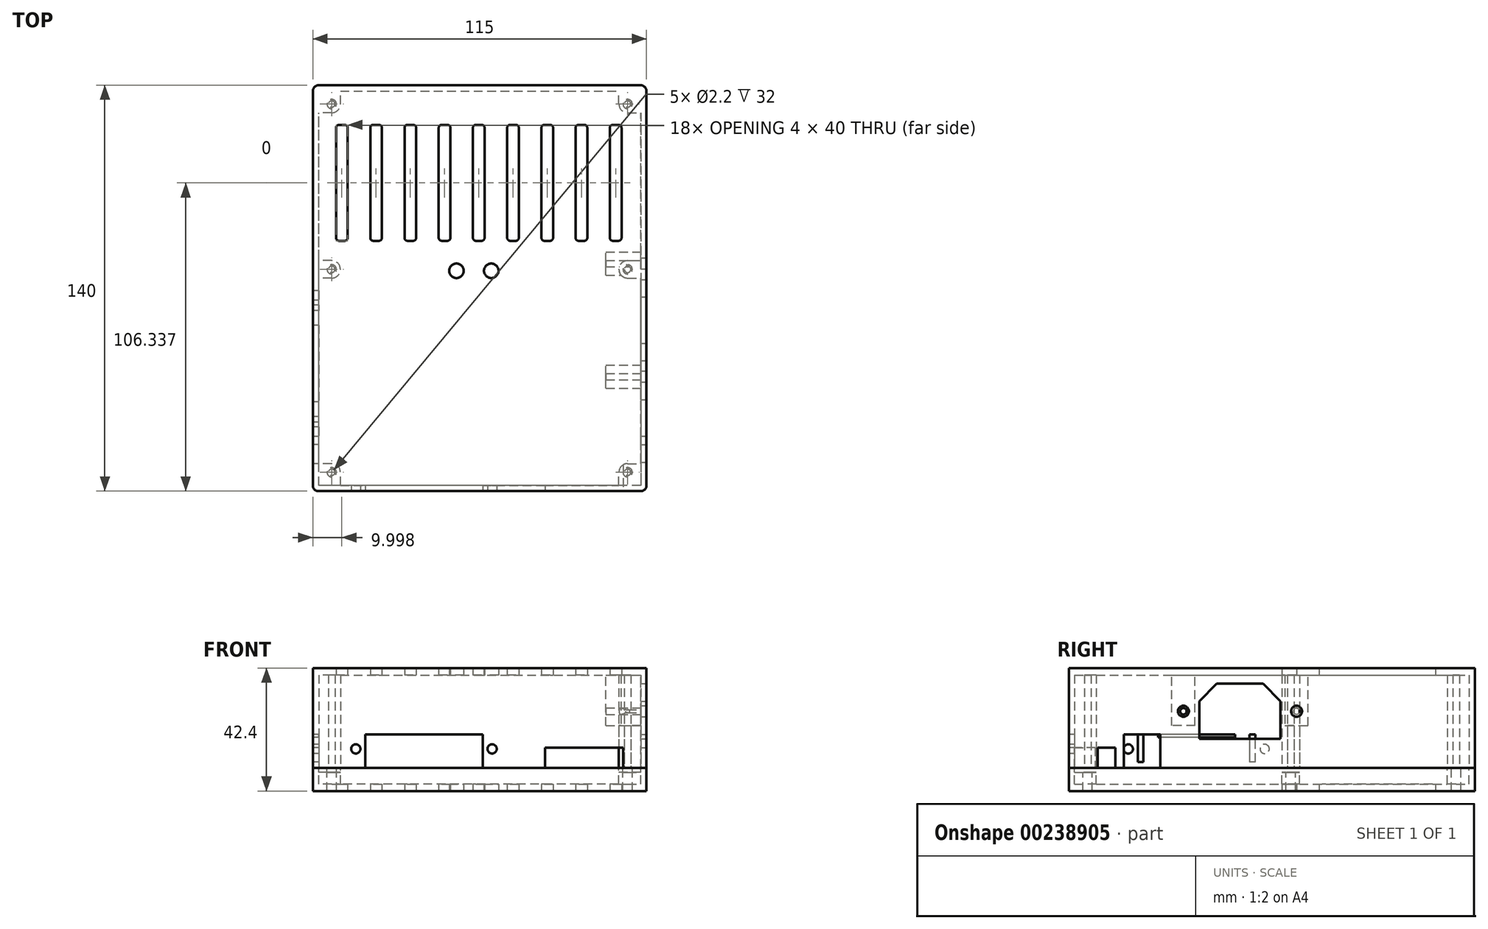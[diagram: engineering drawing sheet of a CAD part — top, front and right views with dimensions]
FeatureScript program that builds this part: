
annotation { "Feature Type Name" : "Feature", "Feature Type Description" : "" }
export const myFeature = defineFeature(function(context is Context, id is Id, definition is map)
    precondition{}
    {
        {
            var Q0;
            Q0=qCreatedBy(makeId("Top.planeOp"),FACE);
            var sketch = newSketch(context, id + "F0", { "sketchPlane" : qUnion([Q0])});
            skLineSegment(sketch, "E0.bottom", {"start": v(7.5, 0) * mm, "end": v(103.5, 0) * mm});
            skLineSegment(sketch, "E0.top", {"start": v(7.5, 136) * mm, "end": v(103.5, 136) * mm});
            skLineSegment(sketch, "E0.left", {"start": v(0, 7.5) * mm, "end": v(0, 71.5) * mm});
            skLineSegment(sketch, "E0.right", {"start": v(111, 7.5) * mm, "end": v(111, 71.5) * mm});
            skCircle(sketch, "E1", {"center": v(4.5, 4.5) * mm, "radius": 1.6 * mm, "construction": true});
            skLineSegment(sketch, "E2", {"start": v(55.5, 0) * mm, "end": v(55.5, 136) * mm, "construction": true});
            skCircle(sketch, "E3", {"center": v(4.5, 74.5) * mm, "radius": 1.6 * mm, "construction": true});
            skCircle(sketch, "E4", {"center": v(4.5, 131.5) * mm, "radius": 1.6 * mm, "construction": true});
            skCircle(sketch, "E5.MirrorC", {"center": v(106.5, 4.5) * mm, "radius": 1.6 * mm, "construction": true});
            skCircle(sketch, "E6.MirrorC", {"center": v(106.5, 74.5) * mm, "radius": 1.6 * mm, "construction": true});
            skCircle(sketch, "E7.MirrorC", {"center": v(106.5, 131.5) * mm, "radius": 1.6 * mm, "construction": true});
            skArc(sketch, "E8", {"start": v(7.5, 4.5) * mm, "mid": v(6.62, 6.62) * mm, "end": v(4.5, 7.5) * mm});
            skArc(sketch, "E9", {"start": v(4.5, 71.5) * mm, "mid": v(7.5, 74.5) * mm, "end": v(4.5, 77.5) * mm});
            skArc(sketch, "E10", {"start": v(4.5, 128.5) * mm, "mid": v(6.62, 129.38) * mm, "end": v(7.5, 131.5) * mm});
            skLineSegment(sketch, "E11", {"start": v(4.5, 7.5) * mm, "end": v(0, 7.5) * mm});
            skLineSegment(sketch, "E12", {"start": v(7.5, 0) * mm, "end": v(7.5, 4.5) * mm});
            skLineSegment(sketch, "E13.0", {"start": v(-2, 0) * mm, "end": v(-2, 136) * mm});
            skLineSegment(sketch, "E13.1", {"start": v(0, -2) * mm, "end": v(111, -2) * mm});
            skLineSegment(sketch, "E13.2", {"start": v(113, 0) * mm, "end": v(113, 136) * mm});
            skLineSegment(sketch, "E13.3", {"start": v(0, 138) * mm, "end": v(111, 138) * mm});
            skLineSegment(sketch, "E14", {"start": v(4.5, 77.5) * mm, "end": v(0, 77.5) * mm});
            skLineSegment(sketch, "E15", {"start": v(4.5, 71.5) * mm, "end": v(0, 71.5) * mm});
            skLineSegment(sketch, "E16", {"start": v(7.5, 131.5) * mm, "end": v(7.5, 136) * mm});
            skLineSegment(sketch, "E17", {"start": v(4.5, 128.5) * mm, "end": v(0, 128.5) * mm});
            skCircle(sketch, "E18", {"center": v(4.5, 4.5) * mm, "radius": 1.1 * mm});
            skCircle(sketch, "E19", {"center": v(4.5, 74.5) * mm, "radius": 1.1 * mm});
            skCircle(sketch, "E20", {"center": v(4.5, 131.5) * mm, "radius": 1.1 * mm});
            skLineSegment(sketch, "E21.MirrorCS", {"start": v(103.5, 0) * mm, "end": v(103.5, 4.5) * mm});
            skCircle(sketch, "E22.MirrorC", {"center": v(106.5, 4.5) * mm, "radius": 1.1 * mm});
            skArc(sketch, "E23.MirrorCS", {"start": v(103.5, 4.5) * mm, "mid": v(104.38, 6.62) * mm, "end": v(106.5, 7.5) * mm});
            skLineSegment(sketch, "E24.MirrorCS", {"start": v(106.5, 7.5) * mm, "end": v(111, 7.5) * mm});
            skLineSegment(sketch, "E25.MirrorCS", {"start": v(106.5, 71.5) * mm, "end": v(111, 71.5) * mm});
            skArc(sketch, "E26.MirrorCS", {"start": v(106.5, 71.5) * mm, "mid": v(103.5, 74.5) * mm, "end": v(106.5, 77.5) * mm});
            skCircle(sketch, "E27.MirrorC", {"center": v(106.5, 74.5) * mm, "radius": 1.1 * mm});
            skLineSegment(sketch, "E28.MirrorCS", {"start": v(106.5, 77.5) * mm, "end": v(111, 77.5) * mm});
            skLineSegment(sketch, "E29.MirrorCS", {"start": v(106.5, 128.5) * mm, "end": v(111, 128.5) * mm});
            skArc(sketch, "E30.MirrorCS", {"start": v(106.5, 128.5) * mm, "mid": v(104.38, 129.38) * mm, "end": v(103.5, 131.5) * mm});
            skLineSegment(sketch, "E31.MirrorCS", {"start": v(103.5, 131.5) * mm, "end": v(103.5, 136) * mm});
            skCircle(sketch, "E32.MirrorC", {"center": v(106.5, 131.5) * mm, "radius": 1.1 * mm});
            skPoint(sketch, "E33.orphan", {"position": v(0, 136) * mm});
            skPoint(sketch, "E34.orphan", {"position": v(111, 136) * mm});
            skPoint(sketch, "E35.orphan", {"position": v(0, 0) * mm});
            skPoint(sketch, "E36.orphan", {"position": v(111, 0) * mm});
            skLineSegment(sketch, "E37.trimOffspring", {"start": v(0, 77.5) * mm, "end": v(0, 128.5) * mm});
            skLineSegment(sketch, "E38.trimOffspring", {"start": v(111, 77.5) * mm, "end": v(111, 128.5) * mm});
            skPoint(sketch, "E39.visualSharp", {"position": v(-2, 138) * mm});
            skArc(sketch, "E39.filletArc", {"start": v(0, 138) * mm, "mid": v(-1.41, 137.41) * mm, "end": v(-2, 136) * mm});
            skPoint(sketch, "E40.visualSharp", {"position": v(113, 138) * mm});
            skArc(sketch, "E40.filletArc", {"start": v(113, 136) * mm, "mid": v(112.41, 137.41) * mm, "end": v(111, 138) * mm});
            skPoint(sketch, "E41.visualSharp", {"position": v(113, -2) * mm});
            skArc(sketch, "E41.filletArc", {"start": v(111, -2) * mm, "mid": v(112.41, -1.41) * mm, "end": v(113, 0) * mm});
            skPoint(sketch, "E42.visualSharp", {"position": v(-2, -2) * mm});
            skArc(sketch, "E42.filletArc", {"start": v(-2, 0) * mm, "mid": v(-1.41, -1.41) * mm, "end": v(0, -2) * mm});
            skSolve(sketch);
        }
        {
            var Q0;
            Q0 = qSketchRegion(id + "F0", true);
            extrude(context, id + "F1", {"entities" : qUnion([Q0]), "depth" : 32 * mm});
        }
        {
            var Q0;
            Q0=makeQuery(id+"F1.opExtrude","CAP_FACE",FACE,{"disambiguationData":[OSD([sQuery(id+"F0.wireOp",EDGE,"E0.bottom"),sQuery(id+"F0.wireOp",EDGE,"E0.top"),sQuery(id+"F0.wireOp",EDGE,"E0.left"),sQuery(id+"F0.wireOp",EDGE,"E0.right"),sQuery(id+"F0.wireOp",EDGE,"E8"),sQuery(id+"F0.wireOp",EDGE,"E9"),sQuery(id+"F0.wireOp",EDGE,"E10"),sQuery(id+"F0.wireOp",EDGE,"E11"),sQuery(id+"F0.wireOp",EDGE,"E12"),sQuery(id+"F0.wireOp",EDGE,"E13.0"),sQuery(id+"F0.wireOp",EDGE,"E13.1"),sQuery(id+"F0.wireOp",EDGE,"E13.2"),sQuery(id+"F0.wireOp",EDGE,"E13.3"),sQuery(id+"F0.wireOp",EDGE,"E14"),sQuery(id+"F0.wireOp",EDGE,"E15"),sQuery(id+"F0.wireOp",EDGE,"E16"),sQuery(id+"F0.wireOp",EDGE,"E17"),sQuery(id+"F0.wireOp",EDGE,"E18"),sQuery(id+"F0.wireOp",EDGE,"E19"),sQuery(id+"F0.wireOp",EDGE,"E20"),sQuery(id+"F0.wireOp",EDGE,"E21.MirrorCS"),sQuery(id+"F0.wireOp",EDGE,"E22.MirrorC"),sQuery(id+"F0.wireOp",EDGE,"E23.MirrorCS"),sQuery(id+"F0.wireOp",EDGE,"E24.MirrorCS"),sQuery(id+"F0.wireOp",EDGE,"E25.MirrorCS"),sQuery(id+"F0.wireOp",EDGE,"E26.MirrorCS"),sQuery(id+"F0.wireOp",EDGE,"E27.MirrorC"),sQuery(id+"F0.wireOp",EDGE,"E28.MirrorCS"),sQuery(id+"F0.wireOp",EDGE,"E29.MirrorCS"),sQuery(id+"F0.wireOp",EDGE,"E30.MirrorCS"),sQuery(id+"F0.wireOp",EDGE,"E31.MirrorCS"),sQuery(id+"F0.wireOp",EDGE,"E32.MirrorC"),sQuery(id+"F0.wireOp",EDGE,"E37.trimOffspring"),sQuery(id+"F0.wireOp",EDGE,"E38.trimOffspring"),sQuery(id+"F0.wireOp",EDGE,"E39.filletArc"),sQuery(id+"F0.wireOp",EDGE,"E40.filletArc"),sQuery(id+"F0.wireOp",EDGE,"E41.filletArc"),sQuery(id+"F0.wireOp",EDGE,"E42.filletArc")])],"isStart":true});
            var sketch = newSketch(context, id + "F2", { "sketchPlane" : qUnion([Q0])});
            skLineSegment(sketch, "E43.0", {"start": v(0, 2) * mm, "end": v(111, 2) * mm});
            skLineSegment(sketch, "E44.0", {"start": v(113, 0) * mm, "end": v(113, -136) * mm});
            skPoint(sketch, "E45.0", {"position": v(112.41, 1.41) * mm});
            skArc(sketch, "E46.0", {"start": v(-2, 0) * mm, "mid": v(-1.41, 1.41) * mm, "end": v(0, 2) * mm});
            skLineSegment(sketch, "E47.0", {"start": v(-2, 0) * mm, "end": v(-2, -136) * mm});
            skArc(sketch, "E48.0", {"start": v(113, -136) * mm, "mid": v(112.41, -137.41) * mm, "end": v(111, -138) * mm});
            skLineSegment(sketch, "E49.0", {"start": v(0, -138) * mm, "end": v(111, -138) * mm});
            skArc(sketch, "E50.0", {"start": v(0, -138) * mm, "mid": v(-1.41, -137.41) * mm, "end": v(-2, -136) * mm});
            skLineSegment(sketch, "E51.0", {"start": v(7.5, -136) * mm, "end": v(103.5, -136) * mm});
            skCircle(sketch, "E52.0", {"center": v(4.5, -131.5) * mm, "radius": 1.1 * mm, "construction": true});
            skCircle(sketch, "E53.0", {"center": v(106.5, -131.5) * mm, "radius": 1.1 * mm, "construction": true});
            skLineSegment(sketch, "E54.0", {"start": v(111, -77.5) * mm, "end": v(111, -128.5) * mm});
            skPoint(sketch, "E55.0", {"position": v(104.38, -129.38) * mm});
            skArc(sketch, "E56.0", {"start": v(106.5, -128.5) * mm, "mid": v(104.38, -129.38) * mm, "end": v(103.5, -131.5) * mm});
            skLineSegment(sketch, "E57.0", {"start": v(103.5, -131.5) * mm, "end": v(103.5, -136) * mm});
            skPoint(sketch, "E58.0", {"position": v(108.75, -128.5) * mm});
            skLineSegment(sketch, "E59.0", {"start": v(106.5, -128.5) * mm, "end": v(111, -128.5) * mm});
            skLineSegment(sketch, "E60.0", {"start": v(7.5, -131.5) * mm, "end": v(7.5, -136) * mm});
            skArc(sketch, "E61.0", {"start": v(4.5, -128.5) * mm, "mid": v(6.62, -129.38) * mm, "end": v(7.5, -131.5) * mm});
            skLineSegment(sketch, "E62.0", {"start": v(4.5, -128.5) * mm, "end": v(0, -128.5) * mm});
            skLineSegment(sketch, "E63.0", {"start": v(0, -77.5) * mm, "end": v(0, -128.5) * mm});
            skPoint(sketch, "E64.0", {"position": v(2.25, -77.5) * mm});
            skLineSegment(sketch, "E65.0", {"start": v(4.5, -77.5) * mm, "end": v(0, -77.5) * mm, "construction": true});
            skArc(sketch, "E66.0", {"start": v(4.5, -71.5) * mm, "mid": v(7.5, -74.5) * mm, "end": v(4.5, -77.5) * mm, "construction": true});
            skCircle(sketch, "E67.0", {"center": v(4.5, -74.5) * mm, "radius": 1.1 * mm, "construction": true});
            skPoint(sketch, "E68.0", {"position": v(2.25, -71.5) * mm});
            skLineSegment(sketch, "E69.0", {"start": v(4.5, -71.5) * mm, "end": v(0, -71.5) * mm, "construction": true});
            skLineSegment(sketch, "E70.0", {"start": v(0, -7.5) * mm, "end": v(0, -71.5) * mm});
            skPoint(sketch, "E71.0", {"position": v(2.25, -7.5) * mm});
            skLineSegment(sketch, "E72.0", {"start": v(4.5, -7.5) * mm, "end": v(0, -7.5) * mm, "construction": true});
            skCircle(sketch, "E73.0", {"center": v(4.5, -4.5) * mm, "radius": 1.1 * mm});
            skPoint(sketch, "E74.0", {"position": v(6.62, -6.62) * mm});
            skArc(sketch, "E75.0", {"start": v(7.5, -4.5) * mm, "mid": v(6.62, -6.62) * mm, "end": v(4.5, -7.5) * mm, "construction": true});
            skLineSegment(sketch, "E76.0", {"start": v(7.5, 0) * mm, "end": v(7.5, -4.5) * mm, "construction": true});
            skLineSegment(sketch, "E77.0", {"start": v(7.5, 0) * mm, "end": v(103.5, 0) * mm});
            skLineSegment(sketch, "E78.0", {"start": v(103.5, 0) * mm, "end": v(103.5, -4.5) * mm, "construction": true});
            skArc(sketch, "E79.0", {"start": v(103.5, -4.5) * mm, "mid": v(104.38, -6.62) * mm, "end": v(106.5, -7.5) * mm, "construction": true});
            skCircle(sketch, "E80.0", {"center": v(106.5, -4.5) * mm, "radius": 1.1 * mm, "construction": true});
            skPoint(sketch, "E81.0", {"position": v(108.75, -7.5) * mm});
            skLineSegment(sketch, "E82.0", {"start": v(106.5, -7.5) * mm, "end": v(111, -7.5) * mm, "construction": true});
            skLineSegment(sketch, "E83.0", {"start": v(111, -7.5) * mm, "end": v(111, -71.5) * mm});
            skLineSegment(sketch, "E84.0", {"start": v(106.5, -71.5) * mm, "end": v(111, -71.5) * mm, "construction": true});
            skLineSegment(sketch, "E85.0", {"start": v(106.5, -77.5) * mm, "end": v(111, -77.5) * mm, "construction": true});
            skArc(sketch, "E86.0", {"start": v(106.5, -71.5) * mm, "mid": v(103.5, -74.5) * mm, "end": v(106.5, -77.5) * mm, "construction": true});
            skCircle(sketch, "E87.0", {"center": v(106.5, -74.5) * mm, "radius": 1.1 * mm, "construction": true});
            skLineSegment(sketch, "E88", {"start": v(0, -7.5) * mm, "end": v(0, 0) * mm});
            skLineSegment(sketch, "E89", {"start": v(7.5, 0) * mm, "end": v(0, 0) * mm});
            skArc(sketch, "E90.0", {"start": v(111, 2) * mm, "mid": v(112.41, 1.41) * mm, "end": v(113, 0) * mm});
            skLineSegment(sketch, "E91", {"start": v(103.5, 0) * mm, "end": v(111, 0) * mm});
            skLineSegment(sketch, "E92", {"start": v(111, -7.5) * mm, "end": v(111, 0) * mm});
            skLineSegment(sketch, "E93", {"start": v(111, -77.5) * mm, "end": v(111, -71.5) * mm});
            skLineSegment(sketch, "E94", {"start": v(0, -71.5) * mm, "end": v(0, -77.5) * mm});
            skCircle(sketch, "E95", {"center": v(4.5, -131.5) * mm, "radius": 1.6 * mm});
            skCircle(sketch, "E96", {"center": v(106.5, -131.5) * mm, "radius": 1.6 * mm});
            skSolve(sketch);
        }
        {
            var Q0;
            Q0 = qSketchRegion(id + "F2", true);
            extrude(context, id + "F3", {"entities" : qUnion([Q0]), "depth" : 1.6 * mm});
        }
        {
            var Q0;
            Q0=makeQuery(id+"F3.opExtrude","CAP_FACE",FACE,{"disambiguationData":[OSD([sQuery(id+"F2.wireOp",EDGE,"E43.0"),sQuery(id+"F2.wireOp",EDGE,"E44.0"),sQuery(id+"F2.wireOp",EDGE,"E46.0"),sQuery(id+"F2.wireOp",EDGE,"E47.0"),sQuery(id+"F2.wireOp",EDGE,"E48.0"),sQuery(id+"F2.wireOp",EDGE,"E49.0"),sQuery(id+"F2.wireOp",EDGE,"E50.0"),sQuery(id+"F2.wireOp",EDGE,"E51.0"),sQuery(id+"F2.wireOp",EDGE,"E54.0"),sQuery(id+"F2.wireOp",EDGE,"E56.0"),sQuery(id+"F2.wireOp",EDGE,"E57.0"),sQuery(id+"F2.wireOp",EDGE,"E59.0"),sQuery(id+"F2.wireOp",EDGE,"E60.0"),sQuery(id+"F2.wireOp",EDGE,"E61.0"),sQuery(id+"F2.wireOp",EDGE,"E62.0"),sQuery(id+"F2.wireOp",EDGE,"E63.0"),sQuery(id+"F2.wireOp",EDGE,"E70.0"),sQuery(id+"F2.wireOp",EDGE,"E77.0"),sQuery(id+"F2.wireOp",EDGE,"E83.0"),sQuery(id+"F2.wireOp",EDGE,"E88"),sQuery(id+"F2.wireOp",EDGE,"E89"),sQuery(id+"F2.wireOp",EDGE,"E90.0"),sQuery(id+"F2.wireOp",EDGE,"E91"),sQuery(id+"F2.wireOp",EDGE,"E92"),sQuery(id+"F2.wireOp",EDGE,"E93"),sQuery(id+"F2.wireOp",EDGE,"E94"),sQuery(id+"F2.wireOp",EDGE,"E95"),sQuery(id+"F2.wireOp",EDGE,"E96")])],"isStart":false});
            var sketch = newSketch(context, id + "F4", { "sketchPlane" : qUnion([Q0])});
            skLineSegment(sketch, "E97.0", {"start": v(0, -138) * mm, "end": v(111, -138) * mm});
            skLineSegment(sketch, "E98.0", {"start": v(7.5, -136) * mm, "end": v(103.5, -136) * mm});
            skLineSegment(sketch, "E99.0", {"start": v(7.5, -131.5) * mm, "end": v(7.5, -136) * mm});
            skArc(sketch, "E100.0", {"start": v(4.5, -128.5) * mm, "mid": v(6.62, -129.38) * mm, "end": v(7.5, -131.5) * mm});
            skLineSegment(sketch, "E101.0", {"start": v(4.5, -128.5) * mm, "end": v(0, -128.5) * mm});
            skCircle(sketch, "E102.0", {"center": v(4.5, -131.5) * mm, "radius": 1.6 * mm});
            skArc(sketch, "E103.0", {"start": v(0, -138) * mm, "mid": v(-1.41, -137.41) * mm, "end": v(-2, -136) * mm});
            skLineSegment(sketch, "E104.0", {"start": v(-2, 0) * mm, "end": v(-2, -136) * mm});
            skLineSegment(sketch, "E105.0", {"start": v(0, -7.5) * mm, "end": v(0, -71.5) * mm});
            skArc(sketch, "E106.0", {"start": v(113, -136) * mm, "mid": v(112.41, -137.41) * mm, "end": v(111, -138) * mm});
            skLineSegment(sketch, "E107.0", {"start": v(113, 0) * mm, "end": v(113, -136) * mm});
            skCircle(sketch, "E108.0", {"center": v(106.5, -131.5) * mm, "radius": 1.6 * mm});
            skLineSegment(sketch, "E109.0", {"start": v(103.5, -131.5) * mm, "end": v(103.5, -136) * mm});
            skArc(sketch, "E110.0", {"start": v(106.5, -128.5) * mm, "mid": v(104.38, -129.38) * mm, "end": v(103.5, -131.5) * mm});
            skLineSegment(sketch, "E111.0", {"start": v(106.5, -128.5) * mm, "end": v(111, -128.5) * mm});
            skLineSegment(sketch, "E112.0", {"start": v(111, -128.5) * mm, "end": v(111, -77.5) * mm});
            skLineSegment(sketch, "E113.0", {"start": v(103.5, 0) * mm, "end": v(7.5, 0) * mm});
            skLineSegment(sketch, "E114.0", {"start": v(0, 2) * mm, "end": v(111, 2) * mm});
            skArc(sketch, "E115.0", {"start": v(111, 2) * mm, "mid": v(112.41, 1.41) * mm, "end": v(113, 0) * mm});
            skArc(sketch, "E116.0", {"start": v(-2, 0) * mm, "mid": v(-1.41, 1.41) * mm, "end": v(0, 2) * mm});
            skCircle(sketch, "E117.0", {"center": v(4.5, -74.5) * mm, "radius": 1.1 * mm, "construction": true});
            skLineSegment(sketch, "E118.0", {"start": v(4.5, -77.5) * mm, "end": v(0, -77.5) * mm});
            skArc(sketch, "E119.0", {"start": v(4.5, -71.5) * mm, "mid": v(7.5, -74.5) * mm, "end": v(4.5, -77.5) * mm});
            skLineSegment(sketch, "E120.0", {"start": v(4.5, -71.5) * mm, "end": v(0, -71.5) * mm});
            skLineSegment(sketch, "E121.0", {"start": v(4.5, -7.5) * mm, "end": v(0, -7.5) * mm});
            skArc(sketch, "E122.0", {"start": v(7.5, -4.5) * mm, "mid": v(6.62, -6.62) * mm, "end": v(4.5, -7.5) * mm});
            skCircle(sketch, "E123.0", {"center": v(4.5, -4.5) * mm, "radius": 1.1 * mm, "construction": true});
            skLineSegment(sketch, "E124.0", {"start": v(7.5, 0) * mm, "end": v(7.5, -4.5) * mm});
            skLineSegment(sketch, "E125.0", {"start": v(106.5, -7.5) * mm, "end": v(111, -7.5) * mm});
            skArc(sketch, "E126.0", {"start": v(103.5, -4.5) * mm, "mid": v(104.38, -6.62) * mm, "end": v(106.5, -7.5) * mm});
            skCircle(sketch, "E127.0", {"center": v(106.5, -4.5) * mm, "radius": 1.1 * mm, "construction": true});
            skLineSegment(sketch, "E128.0", {"start": v(103.5, 0) * mm, "end": v(103.5, -4.5) * mm});
            skLineSegment(sketch, "E129.0", {"start": v(106.5, -77.5) * mm, "end": v(111, -77.5) * mm});
            skArc(sketch, "E130.0", {"start": v(106.5, -71.5) * mm, "mid": v(103.5, -74.5) * mm, "end": v(106.5, -77.5) * mm});
            skCircle(sketch, "E131.0", {"center": v(106.5, -74.5) * mm, "radius": 1.1 * mm, "construction": true});
            skLineSegment(sketch, "E132.0", {"start": v(106.5, -71.5) * mm, "end": v(111, -71.5) * mm});
            skLineSegment(sketch, "E133.trimOffspring", {"start": v(0, -77.5) * mm, "end": v(0, -128.5) * mm});
            skLineSegment(sketch, "E134.trimOffspring", {"start": v(111, -71.5) * mm, "end": v(111, -7.5) * mm});
            skCircle(sketch, "E135", {"center": v(4.5, -4.5) * mm, "radius": 1.6 * mm});
            skCircle(sketch, "E136", {"center": v(106.5, -4.5) * mm, "radius": 1.6 * mm});
            skCircle(sketch, "E137", {"center": v(106.5, -74.5) * mm, "radius": 1.6 * mm});
            skCircle(sketch, "E138", {"center": v(4.5, -74.5) * mm, "radius": 1.6 * mm});
            skSolve(sketch);
        }
        {
            var Q0;
            Q0 = qSketchRegion(id + "F4", true);
            extrude(context, id + "F5", {"entities" : qUnion([Q0]), "operationType" : NewBodyOperationType.ADD, "depth" : 4 * mm});
        }
        {
            var Q0;
            Q0=makeQuery(id+"F5.opExtrude","CAP_FACE",FACE,{"disambiguationData":[OSD([sQuery(id+"F4.wireOp",EDGE,"E97.0"),sQuery(id+"F4.wireOp",EDGE,"E98.0"),sQuery(id+"F4.wireOp",EDGE,"E99.0"),sQuery(id+"F4.wireOp",EDGE,"E100.0"),sQuery(id+"F4.wireOp",EDGE,"E101.0"),sQuery(id+"F4.wireOp",EDGE,"E102.0"),sQuery(id+"F4.wireOp",EDGE,"E103.0"),sQuery(id+"F4.wireOp",EDGE,"E104.0"),sQuery(id+"F4.wireOp",EDGE,"E105.0"),sQuery(id+"F4.wireOp",EDGE,"E106.0"),sQuery(id+"F4.wireOp",EDGE,"E107.0"),sQuery(id+"F4.wireOp",EDGE,"E108.0"),sQuery(id+"F4.wireOp",EDGE,"E109.0"),sQuery(id+"F4.wireOp",EDGE,"E110.0"),sQuery(id+"F4.wireOp",EDGE,"E111.0"),sQuery(id+"F4.wireOp",EDGE,"E112.0"),sQuery(id+"F4.wireOp",EDGE,"E113.0"),sQuery(id+"F4.wireOp",EDGE,"E114.0"),sQuery(id+"F4.wireOp",EDGE,"E115.0"),sQuery(id+"F4.wireOp",EDGE,"E116.0"),sQuery(id+"F4.wireOp",EDGE,"E118.0"),sQuery(id+"F4.wireOp",EDGE,"E119.0"),sQuery(id+"F4.wireOp",EDGE,"E120.0"),sQuery(id+"F4.wireOp",EDGE,"E121.0"),sQuery(id+"F4.wireOp",EDGE,"E122.0"),sQuery(id+"F4.wireOp",EDGE,"E124.0"),sQuery(id+"F4.wireOp",EDGE,"E125.0"),sQuery(id+"F4.wireOp",EDGE,"E126.0"),sQuery(id+"F4.wireOp",EDGE,"E128.0"),sQuery(id+"F4.wireOp",EDGE,"E129.0"),sQuery(id+"F4.wireOp",EDGE,"E130.0"),sQuery(id+"F4.wireOp",EDGE,"E132.0"),sQuery(id+"F4.wireOp",EDGE,"E133.trimOffspring"),sQuery(id+"F4.wireOp",EDGE,"E134.trimOffspring"),sQuery(id+"F4.wireOp",EDGE,"E135"),sQuery(id+"F4.wireOp",EDGE,"E136"),sQuery(id+"F4.wireOp",EDGE,"E137"),sQuery(id+"F4.wireOp",EDGE,"E138")])],"isStart":false});
            var sketch = newSketch(context, id + "F6", { "sketchPlane" : qUnion([Q0])});
            skLineSegment(sketch, "E139.0", {"start": v(0, 2) * mm, "end": v(111, 2) * mm});
            skArc(sketch, "E140.0", {"start": v(-2, 0) * mm, "mid": v(-1.41, 1.41) * mm, "end": v(0, 2) * mm});
            skCircle(sketch, "E141.0", {"center": v(4.5, -4.5) * mm, "radius": 1.6 * mm, "construction": true});
            skLineSegment(sketch, "E142.0", {"start": v(-2, 0) * mm, "end": v(-2, -136) * mm});
            skCircle(sketch, "E143.0", {"center": v(4.5, -74.5) * mm, "radius": 1.6 * mm, "construction": true});
            skCircle(sketch, "E144.0", {"center": v(4.5, -131.5) * mm, "radius": 1.6 * mm, "construction": true});
            skArc(sketch, "E145.0", {"start": v(0, -138) * mm, "mid": v(-1.41, -137.41) * mm, "end": v(-2, -136) * mm});
            skLineSegment(sketch, "E146.0", {"start": v(0, -138) * mm, "end": v(111, -138) * mm});
            skArc(sketch, "E147.0", {"start": v(113, -136) * mm, "mid": v(112.41, -137.41) * mm, "end": v(111, -138) * mm});
            skLineSegment(sketch, "E148.0", {"start": v(113, 0) * mm, "end": v(113, -136) * mm});
            skCircle(sketch, "E149.0", {"center": v(106.5, -131.5) * mm, "radius": 1.6 * mm, "construction": true});
            skCircle(sketch, "E150.0", {"center": v(106.5, -74.5) * mm, "radius": 1.6 * mm, "construction": true});
            skCircle(sketch, "E151.0", {"center": v(106.5, -4.5) * mm, "radius": 1.6 * mm, "construction": true});
            skArc(sketch, "E152.0", {"start": v(111, 2) * mm, "mid": v(112.41, 1.41) * mm, "end": v(113, 0) * mm});
            skCircle(sketch, "E153", {"center": v(4.5, -4.5) * mm, "radius": 1.6 * mm});
            skCircle(sketch, "E154", {"center": v(106.5, -4.5) * mm, "radius": 1.6 * mm});
            skCircle(sketch, "E155", {"center": v(106.5, -74.5) * mm, "radius": 1.6 * mm});
            skCircle(sketch, "E156", {"center": v(106.5, -131.5) * mm, "radius": 1.6 * mm});
            skCircle(sketch, "E157", {"center": v(4.5, -131.5) * mm, "radius": 1.6 * mm});
            skCircle(sketch, "E158", {"center": v(4.5, -74.5) * mm, "radius": 1.6 * mm});
            skSolve(sketch);
        }
        {
            var Q0;
            Q0 = qSketchRegion(id + "F6", true);
            extrude(context, id + "F7", {"entities" : qUnion([Q0]), "operationType" : NewBodyOperationType.ADD, "depth" : 2.4 * mm});
        }
        {
            var Q0;
            Q0=makeQuery(id+"F1.opExtrude","SWEPT_FACE",FACE,{"disambiguationData":[OSD([sQuery(id+"F0.wireOp",EDGE,"E13.1")])]});
            var sketch = newSketch(context, id + "F8", { "sketchPlane" : qUnion([Q0])});
            skLineSegment(sketch, "E159.bottom", {"start": v(105, 7) * mm, "end": v(78, 7) * mm});
            skLineSegment(sketch, "E159.top", {"start": v(105, 0) * mm, "end": v(78, 0) * mm});
            skLineSegment(sketch, "E159.left", {"start": v(105, 7) * mm, "end": v(105, 0) * mm});
            skLineSegment(sketch, "E159.right", {"start": v(78, 7) * mm, "end": v(78, 0) * mm});
            skLineSegment(sketch, "E160.bottom", {"start": v(16.05, 1.5) * mm, "end": v(56.55, 1.5) * mm, "construction": true});
            skLineSegment(sketch, "E160.top", {"start": v(16.05, 11.5) * mm, "end": v(56.55, 11.5) * mm});
            skLineSegment(sketch, "E160.left", {"start": v(16.05, 1.5) * mm, "end": v(16.05, 11.5) * mm});
            skLineSegment(sketch, "E160.right", {"start": v(56.55, 1.5) * mm, "end": v(56.55, 11.5) * mm});
            skLineSegment(sketch, "E161", {"start": v(12.8, 6.5) * mm, "end": v(59.8, 6.5) * mm, "construction": true});
            skCircle(sketch, "E162", {"center": v(59.8, 6.5) * mm, "radius": 1.6 * mm});
            skCircle(sketch, "E163", {"center": v(12.8, 6.5) * mm, "radius": 1.6 * mm});
            skLineSegment(sketch, "E164", {"start": v(36.3, 11.5) * mm, "end": v(36.3, 6.5) * mm, "construction": true});
            skLineSegment(sketch, "E165", {"start": v(16.05, 1.5) * mm, "end": v(16.05, 0) * mm});
            skLineSegment(sketch, "E166", {"start": v(16.05, 0) * mm, "end": v(56.55, 0) * mm});
            skLineSegment(sketch, "E167", {"start": v(56.55, 0) * mm, "end": v(56.55, 1.5) * mm});
            skSolve(sketch);
        }
        {
            var Q0;
            Q0 = qSketchRegion(id + "F8", true);
            extrude(context, id + "F9", {"entities" : qUnion([Q0]), "operationType" : NewBodyOperationType.REMOVE, "oppositeDirection" : true, "depth" : 25 * mm});
        }
        {
            var Q0;
            Q0=makeQuery(id+"F1.opExtrude","SWEPT_FACE",FACE,{"disambiguationData":[OSD([sQuery(id+"F0.wireOp",EDGE,"E13.0")])]});
            var sketch = newSketch(context, id + "F10", { "sketchPlane" : qUnion([Q0])});
            skLineSegment(sketch, "E168.bottom", {"start": v(-7.5, 7) * mm, "end": v(-14, 7) * mm});
            skLineSegment(sketch, "E168.top", {"start": v(-7.5, 0) * mm, "end": v(-14, 0) * mm});
            skLineSegment(sketch, "E168.left", {"start": v(-7.5, 7) * mm, "end": v(-7.5, 0) * mm});
            skLineSegment(sketch, "E168.right", {"start": v(-14, 7) * mm, "end": v(-14, 0) * mm});
            skLineSegment(sketch, "E169.top", {"start": v(-62.25, 11.5) * mm, "end": v(-60.25, 11.5) * mm});
            skLineSegment(sketch, "E169.left", {"start": v(-62.25, 2) * mm, "end": v(-62.25, 11.5) * mm});
            skLineSegment(sketch, "E169.right", {"start": v(-21.75, 2) * mm, "end": v(-21.75, 11.5) * mm});
            skLineSegment(sketch, "E170", {"start": v(-65.5, 6.5) * mm, "end": v(-18.5, 6.5) * mm, "construction": true});
            skCircle(sketch, "E171", {"center": v(-18.5, 6.5) * mm, "radius": 1.6 * mm});
            skCircle(sketch, "E172", {"center": v(-65.5, 6.5) * mm, "radius": 1.6 * mm});
            skLineSegment(sketch, "E173", {"start": v(-42, 11.5) * mm, "end": v(-42, 6.5) * mm, "construction": true});
            skLineSegment(sketch, "E174.bottom", {"start": v(-55.25, 10.5) * mm, "end": v(-28.75, 10.5) * mm});
            skLineSegment(sketch, "E174.left", {"start": v(-60.25, 10.5) * mm, "end": v(-60.25, 2) * mm});
            skLineSegment(sketch, "E174.right", {"start": v(-23.75, 10.5) * mm, "end": v(-23.75, 2) * mm});
            skLineSegment(sketch, "E175", {"start": v(-60.25, 10.5) * mm, "end": v(-60.25, 11.5) * mm});
            skLineSegment(sketch, "E176", {"start": v(-55.25, 10.5) * mm, "end": v(-55.25, 11.5) * mm});
            skLineSegment(sketch, "E177.MirrorCS", {"start": v(-28.75, 10.5) * mm, "end": v(-28.75, 11.5) * mm});
            skLineSegment(sketch, "E178.MirrorCS", {"start": v(-23.75, 10.5) * mm, "end": v(-23.75, 11.5) * mm});
            skLineSegment(sketch, "E179.trimOffspring", {"start": v(-55.25, 11.5) * mm, "end": v(-28.75, 11.5) * mm});
            skLineSegment(sketch, "E180.trimOffspring", {"start": v(-23.75, 11.5) * mm, "end": v(-21.75, 11.5) * mm});
            skLineSegment(sketch, "E181", {"start": v(-21.75, 2) * mm, "end": v(-23.75, 2) * mm});
            skLineSegment(sketch, "E182", {"start": v(-62.25, 2) * mm, "end": v(-60.25, 2) * mm});
            skSolve(sketch);
        }
        {
            var Q0;
            Q0 = qSketchRegion(id + "F10", true);
            extrude(context, id + "F11", {"entities" : qUnion([Q0]), "operationType" : NewBodyOperationType.REMOVE, "oppositeDirection" : true, "depth" : 25 * mm});
        }
        {
            var Q0;
            Q0=makeQuery(id+"F1.opExtrude","SWEPT_FACE",FACE,{"disambiguationData":[OSD([sQuery(id+"F0.wireOp",EDGE,"E13.2")])]});
            var sketch = newSketch(context, id + "F12", { "sketchPlane" : qUnion([Q0])});
            skLineSegment(sketch, "E183.bottom", {"start": v(8, 0) * mm, "end": v(14, 0) * mm});
            skLineSegment(sketch, "E183.top", {"start": v(8, 7) * mm, "end": v(14, 7) * mm});
            skLineSegment(sketch, "E183.left", {"start": v(8, 0) * mm, "end": v(8, 7) * mm});
            skLineSegment(sketch, "E183.right", {"start": v(14, 0) * mm, "end": v(14, 7) * mm});
            skLineSegment(sketch, "E184.bottom", {"start": v(17, 0) * mm, "end": v(29.5, 0) * mm});
            skLineSegment(sketch, "E184.top", {"start": v(17, 11.5) * mm, "end": v(29.5, 11.5) * mm});
            skLineSegment(sketch, "E184.left", {"start": v(17, 0) * mm, "end": v(17, 11.5) * mm});
            skLineSegment(sketch, "E184.right", {"start": v(29.5, 0) * mm, "end": v(29.5, 11.5) * mm});
            skLineSegment(sketch, "E185", {"start": v(49, 29) * mm, "end": v(65, 29) * mm});
            skLineSegment(sketch, "E186", {"start": v(43, 10) * mm, "end": v(71, 10) * mm});
            skLineSegment(sketch, "E187", {"start": v(57, 29) * mm, "end": v(57, 10) * mm, "construction": true});
            skLineSegment(sketch, "E188", {"start": v(43, 10) * mm, "end": v(43, 23) * mm});
            skLineSegment(sketch, "E189", {"start": v(43, 23) * mm, "end": v(49, 29) * mm});
            skLineSegment(sketch, "E190.MirrorCS", {"start": v(71, 10) * mm, "end": v(71, 23) * mm});
            skLineSegment(sketch, "E191.MirrorCS", {"start": v(71, 23) * mm, "end": v(65, 29) * mm});
            skLineSegment(sketch, "E192", {"start": v(57, 19.5) * mm, "end": v(76.5, 19.5) * mm, "construction": true});
            skCircle(sketch, "E193", {"center": v(76.5, 19.5) * mm, "radius": 1.9 * mm});
            skCircle(sketch, "E194.MirrorC", {"center": v(37.5, 19.5) * mm, "radius": 1.9 * mm});
            skSolve(sketch);
        }
        {
            var Q0;
            Q0 = qSketchRegion(id + "F12", true);
            extrude(context, id + "F13", {"entities" : qUnion([Q0]), "operationType" : NewBodyOperationType.REMOVE, "oppositeDirection" : true, "depth" : 2 * mm});
        }
        {
            var Q0;
            Q0=makeQuery(id+"F1.opExtrude","SWEPT_FACE",FACE,{"disambiguationData":[OSD([sQuery(id+"F0.wireOp",EDGE,"E0.right")])]});
            var sketch = newSketch(context, id + "F14", { "sketchPlane" : qUnion([Q0])});
            skCircle(sketch, "E195.0", {"center": v(-37.5, 19.5) * mm, "radius": 1.9 * mm, "construction": true});
            skArc(sketch, "E196.0", {"start": v(-77.5, 17.88) * mm, "mid": v(-78.4, 19.5) * mm, "end": v(-77.5, 21.12) * mm, "construction": true});
            skLineSegment(sketch, "E197.0", {"start": v(-43, 10) * mm, "end": v(-43, 23) * mm, "construction": true});
            skLineSegment(sketch, "E198.0", {"start": v(-7.5, 32) * mm, "end": v(-71.5, 32) * mm, "construction": true});
            skCircle(sketch, "E199", {"center": v(-37.5, 19.5) * mm, "radius": 1.1 * mm});
            skCircle(sketch, "E200", {"center": v(-76.5, 19.5) * mm, "radius": 1.1 * mm});
            skLineSegment(sketch, "E201.bottom", {"start": v(-41.5, 14.5) * mm, "end": v(-33.5, 14.5) * mm});
            skLineSegment(sketch, "E201.top", {"start": v(-41.5, 32) * mm, "end": v(-33.5, 32) * mm});
            skLineSegment(sketch, "E201.left", {"start": v(-41.5, 14.5) * mm, "end": v(-41.5, 32) * mm});
            skLineSegment(sketch, "E201.right", {"start": v(-33.5, 14.5) * mm, "end": v(-33.5, 32) * mm});
            skLineSegment(sketch, "E202", {"start": v(-37.5, 19.5) * mm, "end": v(-37.5, 14.5) * mm, "construction": true});
            skLineSegment(sketch, "E203", {"start": v(-76.5, 19.5) * mm, "end": v(-37.5, 19.5) * mm, "construction": true});
            skLineSegment(sketch, "E204", {"start": v(-57, 19.5) * mm, "end": v(-57, 26.96) * mm, "construction": true});
            skLineSegment(sketch, "E205.MirrorCS", {"start": v(-80.5, 14.5) * mm, "end": v(-80.5, 32) * mm});
            skLineSegment(sketch, "E206.MirrorCS", {"start": v(-72.5, 32) * mm, "end": v(-80.5, 32) * mm});
            skLineSegment(sketch, "E207.MirrorCS", {"start": v(-72.5, 14.5) * mm, "end": v(-72.5, 32) * mm});
            skLineSegment(sketch, "E208.MirrorCS", {"start": v(-72.5, 14.5) * mm, "end": v(-80.5, 14.5) * mm});
            skSolve(sketch);
        }
        {
            var Q0;
            Q0 = qSketchRegion(id + "F14", true);
            extrude(context, id + "F15", {"entities" : qUnion([Q0]), "operationType" : NewBodyOperationType.ADD, "depth" : 12 * mm});
        }
        {
            var Q0;
            Q0=makeQuery(id+"F15.boolean.opBoolean","MERGE",FACE,{"derivedFrom":[makeQuery(id+"F1.opExtrude","CAP_FACE",FACE,{"disambiguationData":[OSD([sQuery(id+"F0.wireOp",EDGE,"E0.bottom"),sQuery(id+"F0.wireOp",EDGE,"E0.top"),sQuery(id+"F0.wireOp",EDGE,"E0.left"),sQuery(id+"F0.wireOp",EDGE,"E0.right"),sQuery(id+"F0.wireOp",EDGE,"E8"),sQuery(id+"F0.wireOp",EDGE,"E9"),sQuery(id+"F0.wireOp",EDGE,"E10"),sQuery(id+"F0.wireOp",EDGE,"E11"),sQuery(id+"F0.wireOp",EDGE,"E12"),sQuery(id+"F0.wireOp",EDGE,"E13.0"),sQuery(id+"F0.wireOp",EDGE,"E13.1"),sQuery(id+"F0.wireOp",EDGE,"E13.2"),sQuery(id+"F0.wireOp",EDGE,"E13.3"),sQuery(id+"F0.wireOp",EDGE,"E14"),sQuery(id+"F0.wireOp",EDGE,"E15"),sQuery(id+"F0.wireOp",EDGE,"E16"),sQuery(id+"F0.wireOp",EDGE,"E17"),sQuery(id+"F0.wireOp",EDGE,"E18"),sQuery(id+"F0.wireOp",EDGE,"E19"),sQuery(id+"F0.wireOp",EDGE,"E20"),sQuery(id+"F0.wireOp",EDGE,"E21.MirrorCS"),sQuery(id+"F0.wireOp",EDGE,"E22.MirrorC"),sQuery(id+"F0.wireOp",EDGE,"E23.MirrorCS"),sQuery(id+"F0.wireOp",EDGE,"E24.MirrorCS"),sQuery(id+"F0.wireOp",EDGE,"E25.MirrorCS"),sQuery(id+"F0.wireOp",EDGE,"E26.MirrorCS"),sQuery(id+"F0.wireOp",EDGE,"E27.MirrorC"),sQuery(id+"F0.wireOp",EDGE,"E28.MirrorCS"),sQuery(id+"F0.wireOp",EDGE,"E29.MirrorCS"),sQuery(id+"F0.wireOp",EDGE,"E30.MirrorCS"),sQuery(id+"F0.wireOp",EDGE,"E31.MirrorCS"),sQuery(id+"F0.wireOp",EDGE,"E32.MirrorC"),sQuery(id+"F0.wireOp",EDGE,"E37.trimOffspring"),sQuery(id+"F0.wireOp",EDGE,"E38.trimOffspring"),sQuery(id+"F0.wireOp",EDGE,"E39.filletArc"),sQuery(id+"F0.wireOp",EDGE,"E40.filletArc"),sQuery(id+"F0.wireOp",EDGE,"E41.filletArc"),sQuery(id+"F0.wireOp",EDGE,"E42.filletArc")])],"isStart":false}),makeQuery(id+"F15.opExtrude","SWEPT_FACE",FACE,{"disambiguationData":[OSD([sQuery(id+"F14.wireOp",EDGE,"E201.top")])]}),makeQuery(id+"F15.opExtrude","SWEPT_FACE",FACE,{"disambiguationData":[OSD([sQuery(id+"F14.wireOp",EDGE,"E206.MirrorCS")])]})]});
            var sketch = newSketch(context, id + "F16", { "sketchPlane" : qUnion([Q0])});
            skLineSegment(sketch, "E209.0", {"start": v(0, 138) * mm, "end": v(111, 138) * mm});
            skPoint(sketch, "E210.0", {"position": v(112.41, 137.41) * mm});
            skLineSegment(sketch, "E211.0", {"start": v(113, 0) * mm, "end": v(113, 136) * mm});
            skArc(sketch, "E212.0", {"start": v(113, 136) * mm, "mid": v(112.41, 137.41) * mm, "end": v(111, 138) * mm});
            skArc(sketch, "E213.0", {"start": v(111, -2) * mm, "mid": v(112.41, -1.41) * mm, "end": v(113, 0) * mm});
            skLineSegment(sketch, "E214.0", {"start": v(0, -2) * mm, "end": v(111, -2) * mm});
            skArc(sketch, "E215.0", {"start": v(-2, 0) * mm, "mid": v(-1.41, -1.41) * mm, "end": v(0, -2) * mm});
            skLineSegment(sketch, "E216.0", {"start": v(-2, 0) * mm, "end": v(-2, 136) * mm});
            skArc(sketch, "E217.0", {"start": v(0, 138) * mm, "mid": v(-1.41, 137.41) * mm, "end": v(-2, 136) * mm});
            skSolve(sketch);
        }
        {
            var Q0;
            Q0 = qSketchRegion(id + "F16", true);
            extrude(context, id + "F17", {"entities" : qUnion([Q0]), "operationType" : NewBodyOperationType.ADD, "depth" : 2.4 * mm});
        }
        {
            var Q0;
            Q0=makeQuery(id+"F17.boolean.opBoolean","SPLIT",FACE,{"disambiguationData":[TD([makeQuery(id+"F1.opExtrude","SWEPT_FACE",FACE,{"disambiguationData":[OSD([sQuery(id+"F0.wireOp",EDGE,"E0.bottom")])]})])],"derivedFrom":makeQuery(id+"F17.opExtrude","CAP_FACE",FACE,{"disambiguationData":[OSD([sQuery(id+"F16.wireOp",EDGE,"E209.0"),sQuery(id+"F16.wireOp",EDGE,"E211.0"),sQuery(id+"F16.wireOp",EDGE,"E212.0"),sQuery(id+"F16.wireOp",EDGE,"E213.0"),sQuery(id+"F16.wireOp",EDGE,"E214.0"),sQuery(id+"F16.wireOp",EDGE,"E215.0"),sQuery(id+"F16.wireOp",EDGE,"E216.0"),sQuery(id+"F16.wireOp",EDGE,"E217.0")])],"isStart":true})});
            var sketch = newSketch(context, id + "F18", { "sketchPlane" : qUnion([Q0])});
            skLineSegment(sketch, "E218", {"start": v(111, -74) * mm, "end": v(0, -74) * mm, "construction": true});
            skCircle(sketch, "E219", {"center": v(47.5, -74) * mm, "radius": 2.5 * mm});
            skCircle(sketch, "E220", {"center": v(59.5, -74) * mm, "radius": 2.5 * mm});
            skLineSegment(sketch, "E221.bottom", {"start": v(7, -124.34) * mm, "end": v(9, -124.34) * mm});
            skLineSegment(sketch, "E221.top", {"start": v(7, -84.34) * mm, "end": v(9, -84.34) * mm});
            skLineSegment(sketch, "E221.left", {"start": v(6, -123.34) * mm, "end": v(6, -85.34) * mm});
            skLineSegment(sketch, "E221.right", {"start": v(10, -123.34) * mm, "end": v(10, -85.34) * mm});
            skPoint(sketch, "E222.visualSharp", {"position": v(6, -84.34) * mm});
            skArc(sketch, "E222.filletArc", {"start": v(7, -84.34) * mm, "mid": v(6.3, -84.63) * mm, "end": v(6, -85.34) * mm});
            skPoint(sketch, "E223.visualSharp", {"position": v(10, -84.34) * mm});
            skArc(sketch, "E223.filletArc", {"start": v(10, -85.34) * mm, "mid": v(9.7, -84.63) * mm, "end": v(9, -84.34) * mm});
            skPoint(sketch, "E224.visualSharp", {"position": v(6, -124.34) * mm});
            skArc(sketch, "E224.filletArc", {"start": v(6, -123.34) * mm, "mid": v(6.3, -124.04) * mm, "end": v(7, -124.34) * mm});
            skPoint(sketch, "E225.visualSharp", {"position": v(10, -124.34) * mm});
            skArc(sketch, "E225.filletArc", {"start": v(9, -124.34) * mm, "mid": v(9.7, -124.04) * mm, "end": v(10, -123.34) * mm});
            skLineSegment(sketch, "E226.1.0.0", {"start": v(21.8, -123.34) * mm, "end": v(21.8, -85.34) * mm});
            skLineSegment(sketch, "E226.1.0.1", {"start": v(17.8, -123.34) * mm, "end": v(17.8, -85.34) * mm});
            skPoint(sketch, "E226.1.0.2", {"position": v(17.8, -124.34) * mm});
            skPoint(sketch, "E226.1.0.3", {"position": v(21.8, -124.34) * mm});
            skPoint(sketch, "E226.1.0.4", {"position": v(21.8, -84.34) * mm});
            skPoint(sketch, "E226.1.0.5", {"position": v(17.8, -84.34) * mm});
            skLineSegment(sketch, "E226.1.0.6", {"start": v(18.8, -84.34) * mm, "end": v(20.8, -84.34) * mm});
            skArc(sketch, "E226.1.0.7", {"start": v(18.8, -84.34) * mm, "mid": v(18.1, -84.63) * mm, "end": v(17.8, -85.34) * mm});
            skArc(sketch, "E226.1.0.8", {"start": v(21.8, -85.34) * mm, "mid": v(21.5, -84.63) * mm, "end": v(20.8, -84.34) * mm});
            skArc(sketch, "E226.1.0.9", {"start": v(17.8, -123.34) * mm, "mid": v(18.1, -124.04) * mm, "end": v(18.8, -124.34) * mm});
            skArc(sketch, "E226.1.0.10", {"start": v(20.8, -124.34) * mm, "mid": v(21.5, -124.04) * mm, "end": v(21.8, -123.34) * mm});
            skLineSegment(sketch, "E226.1.0.11", {"start": v(18.8, -124.34) * mm, "end": v(20.8, -124.34) * mm});
            skLineSegment(sketch, "E226.2.0.0", {"start": v(33.6, -123.34) * mm, "end": v(33.6, -85.34) * mm});
            skLineSegment(sketch, "E226.2.0.1", {"start": v(29.6, -123.34) * mm, "end": v(29.6, -85.34) * mm});
            skPoint(sketch, "E226.2.0.2", {"position": v(29.6, -124.34) * mm});
            skPoint(sketch, "E226.2.0.3", {"position": v(33.6, -124.34) * mm});
            skPoint(sketch, "E226.2.0.4", {"position": v(33.6, -84.34) * mm});
            skPoint(sketch, "E226.2.0.5", {"position": v(29.6, -84.34) * mm});
            skLineSegment(sketch, "E226.2.0.6", {"start": v(30.6, -84.34) * mm, "end": v(32.6, -84.34) * mm});
            skArc(sketch, "E226.2.0.7", {"start": v(30.6, -84.34) * mm, "mid": v(29.9, -84.63) * mm, "end": v(29.6, -85.34) * mm});
            skArc(sketch, "E226.2.0.8", {"start": v(33.6, -85.34) * mm, "mid": v(33.3, -84.63) * mm, "end": v(32.6, -84.34) * mm});
            skArc(sketch, "E226.2.0.9", {"start": v(29.6, -123.34) * mm, "mid": v(29.9, -124.04) * mm, "end": v(30.6, -124.34) * mm});
            skArc(sketch, "E226.2.0.10", {"start": v(32.6, -124.34) * mm, "mid": v(33.3, -124.04) * mm, "end": v(33.6, -123.34) * mm});
            skLineSegment(sketch, "E226.2.0.11", {"start": v(30.6, -124.34) * mm, "end": v(32.6, -124.34) * mm});
            skLineSegment(sketch, "E226.3.0.0", {"start": v(45.4, -123.34) * mm, "end": v(45.4, -85.34) * mm});
            skLineSegment(sketch, "E226.3.0.1", {"start": v(41.4, -123.34) * mm, "end": v(41.4, -85.34) * mm});
            skPoint(sketch, "E226.3.0.2", {"position": v(41.4, -124.34) * mm});
            skPoint(sketch, "E226.3.0.3", {"position": v(45.4, -124.34) * mm});
            skPoint(sketch, "E226.3.0.4", {"position": v(45.4, -84.34) * mm});
            skPoint(sketch, "E226.3.0.5", {"position": v(41.4, -84.34) * mm});
            skLineSegment(sketch, "E226.3.0.6", {"start": v(42.4, -84.34) * mm, "end": v(44.4, -84.34) * mm});
            skArc(sketch, "E226.3.0.7", {"start": v(42.4, -84.34) * mm, "mid": v(41.7, -84.63) * mm, "end": v(41.4, -85.34) * mm});
            skArc(sketch, "E226.3.0.8", {"start": v(45.4, -85.34) * mm, "mid": v(45.1, -84.63) * mm, "end": v(44.4, -84.34) * mm});
            skArc(sketch, "E226.3.0.9", {"start": v(41.4, -123.34) * mm, "mid": v(41.7, -124.04) * mm, "end": v(42.4, -124.34) * mm});
            skArc(sketch, "E226.3.0.10", {"start": v(44.4, -124.34) * mm, "mid": v(45.1, -124.04) * mm, "end": v(45.4, -123.34) * mm});
            skLineSegment(sketch, "E226.3.0.11", {"start": v(42.4, -124.34) * mm, "end": v(44.4, -124.34) * mm});
            skLineSegment(sketch, "E226.4.0.0", {"start": v(57.2, -123.34) * mm, "end": v(57.2, -85.34) * mm});
            skLineSegment(sketch, "E226.4.0.1", {"start": v(53.2, -123.34) * mm, "end": v(53.2, -85.34) * mm});
            skPoint(sketch, "E226.4.0.2", {"position": v(53.2, -124.34) * mm});
            skPoint(sketch, "E226.4.0.3", {"position": v(57.2, -124.34) * mm});
            skPoint(sketch, "E226.4.0.4", {"position": v(57.2, -84.34) * mm});
            skPoint(sketch, "E226.4.0.5", {"position": v(53.2, -84.34) * mm});
            skLineSegment(sketch, "E226.4.0.6", {"start": v(54.2, -84.34) * mm, "end": v(56.2, -84.34) * mm});
            skArc(sketch, "E226.4.0.7", {"start": v(54.2, -84.34) * mm, "mid": v(53.5, -84.63) * mm, "end": v(53.2, -85.34) * mm});
            skArc(sketch, "E226.4.0.8", {"start": v(57.2, -85.34) * mm, "mid": v(56.9, -84.63) * mm, "end": v(56.2, -84.34) * mm});
            skArc(sketch, "E226.4.0.9", {"start": v(53.2, -123.34) * mm, "mid": v(53.5, -124.04) * mm, "end": v(54.2, -124.34) * mm});
            skArc(sketch, "E226.4.0.10", {"start": v(56.2, -124.34) * mm, "mid": v(56.9, -124.04) * mm, "end": v(57.2, -123.34) * mm});
            skLineSegment(sketch, "E226.4.0.11", {"start": v(54.2, -124.34) * mm, "end": v(56.2, -124.34) * mm});
            skLineSegment(sketch, "E226.5.0.0", {"start": v(69, -123.34) * mm, "end": v(69, -85.34) * mm});
            skLineSegment(sketch, "E226.5.0.1", {"start": v(65, -123.34) * mm, "end": v(65, -85.34) * mm});
            skPoint(sketch, "E226.5.0.2", {"position": v(65, -124.34) * mm});
            skPoint(sketch, "E226.5.0.3", {"position": v(69, -124.34) * mm});
            skPoint(sketch, "E226.5.0.4", {"position": v(69, -84.34) * mm});
            skPoint(sketch, "E226.5.0.5", {"position": v(65, -84.34) * mm});
            skLineSegment(sketch, "E226.5.0.6", {"start": v(66, -84.34) * mm, "end": v(68, -84.34) * mm});
            skArc(sketch, "E226.5.0.7", {"start": v(66, -84.34) * mm, "mid": v(65.3, -84.63) * mm, "end": v(65, -85.34) * mm});
            skArc(sketch, "E226.5.0.8", {"start": v(69, -85.34) * mm, "mid": v(68.7, -84.63) * mm, "end": v(68, -84.34) * mm});
            skArc(sketch, "E226.5.0.9", {"start": v(65, -123.34) * mm, "mid": v(65.3, -124.04) * mm, "end": v(66, -124.34) * mm});
            skArc(sketch, "E226.5.0.10", {"start": v(68, -124.34) * mm, "mid": v(68.7, -124.04) * mm, "end": v(69, -123.34) * mm});
            skLineSegment(sketch, "E226.5.0.11", {"start": v(66, -124.34) * mm, "end": v(68, -124.34) * mm});
            skLineSegment(sketch, "E226.6.0.0", {"start": v(80.8, -123.34) * mm, "end": v(80.8, -85.34) * mm});
            skLineSegment(sketch, "E226.6.0.1", {"start": v(76.8, -123.34) * mm, "end": v(76.8, -85.34) * mm});
            skPoint(sketch, "E226.6.0.2", {"position": v(76.8, -124.34) * mm});
            skPoint(sketch, "E226.6.0.3", {"position": v(80.8, -124.34) * mm});
            skPoint(sketch, "E226.6.0.4", {"position": v(80.8, -84.34) * mm});
            skPoint(sketch, "E226.6.0.5", {"position": v(76.8, -84.34) * mm});
            skLineSegment(sketch, "E226.6.0.6", {"start": v(77.8, -84.34) * mm, "end": v(79.8, -84.34) * mm});
            skArc(sketch, "E226.6.0.7", {"start": v(77.8, -84.34) * mm, "mid": v(77.1, -84.63) * mm, "end": v(76.8, -85.34) * mm});
            skArc(sketch, "E226.6.0.8", {"start": v(80.8, -85.34) * mm, "mid": v(80.5, -84.63) * mm, "end": v(79.8, -84.34) * mm});
            skArc(sketch, "E226.6.0.9", {"start": v(76.8, -123.34) * mm, "mid": v(77.1, -124.04) * mm, "end": v(77.8, -124.34) * mm});
            skArc(sketch, "E226.6.0.10", {"start": v(79.8, -124.34) * mm, "mid": v(80.5, -124.04) * mm, "end": v(80.8, -123.34) * mm});
            skLineSegment(sketch, "E226.6.0.11", {"start": v(77.8, -124.34) * mm, "end": v(79.8, -124.34) * mm});
            skLineSegment(sketch, "E226.7.0.0", {"start": v(92.6, -123.34) * mm, "end": v(92.6, -85.34) * mm});
            skLineSegment(sketch, "E226.7.0.1", {"start": v(88.6, -123.34) * mm, "end": v(88.6, -85.34) * mm});
            skPoint(sketch, "E226.7.0.2", {"position": v(88.6, -124.34) * mm});
            skPoint(sketch, "E226.7.0.3", {"position": v(92.6, -124.34) * mm});
            skPoint(sketch, "E226.7.0.4", {"position": v(92.6, -84.34) * mm});
            skPoint(sketch, "E226.7.0.5", {"position": v(88.6, -84.34) * mm});
            skLineSegment(sketch, "E226.7.0.6", {"start": v(89.6, -84.34) * mm, "end": v(91.6, -84.34) * mm});
            skArc(sketch, "E226.7.0.7", {"start": v(89.6, -84.34) * mm, "mid": v(88.9, -84.63) * mm, "end": v(88.6, -85.34) * mm});
            skArc(sketch, "E226.7.0.8", {"start": v(92.6, -85.34) * mm, "mid": v(92.3, -84.63) * mm, "end": v(91.6, -84.34) * mm});
            skArc(sketch, "E226.7.0.9", {"start": v(88.6, -123.34) * mm, "mid": v(88.9, -124.04) * mm, "end": v(89.6, -124.34) * mm});
            skArc(sketch, "E226.7.0.10", {"start": v(91.6, -124.34) * mm, "mid": v(92.3, -124.04) * mm, "end": v(92.6, -123.34) * mm});
            skLineSegment(sketch, "E226.7.0.11", {"start": v(89.6, -124.34) * mm, "end": v(91.6, -124.34) * mm});
            skLineSegment(sketch, "E226.8.0.0", {"start": v(104.4, -123.34) * mm, "end": v(104.4, -85.34) * mm});
            skLineSegment(sketch, "E226.8.0.1", {"start": v(100.4, -123.34) * mm, "end": v(100.4, -85.34) * mm});
            skPoint(sketch, "E226.8.0.2", {"position": v(100.4, -124.34) * mm});
            skPoint(sketch, "E226.8.0.3", {"position": v(104.4, -124.34) * mm});
            skPoint(sketch, "E226.8.0.4", {"position": v(104.4, -84.34) * mm});
            skPoint(sketch, "E226.8.0.5", {"position": v(100.4, -84.34) * mm});
            skLineSegment(sketch, "E226.8.0.6", {"start": v(101.4, -84.34) * mm, "end": v(103.4, -84.34) * mm});
            skArc(sketch, "E226.8.0.7", {"start": v(101.4, -84.34) * mm, "mid": v(100.7, -84.63) * mm, "end": v(100.4, -85.34) * mm});
            skArc(sketch, "E226.8.0.8", {"start": v(104.4, -85.34) * mm, "mid": v(104.1, -84.63) * mm, "end": v(103.4, -84.34) * mm});
            skArc(sketch, "E226.8.0.9", {"start": v(100.4, -123.34) * mm, "mid": v(100.7, -124.04) * mm, "end": v(101.4, -124.34) * mm});
            skArc(sketch, "E226.8.0.10", {"start": v(103.4, -124.34) * mm, "mid": v(104.1, -124.04) * mm, "end": v(104.4, -123.34) * mm});
            skLineSegment(sketch, "E226.8.0.11", {"start": v(101.4, -124.34) * mm, "end": v(103.4, -124.34) * mm});
            skLineSegment(sketch, "E226.direction1", {"start": v(6, -124.34) * mm, "end": v(17.8, -124.34) * mm, "construction": true});
            skSolve(sketch);
        }
        {
            var Q0;
            Q0 = qSketchRegion(id + "F18", true);
            extrude(context, id + "F19", {"entities" : qUnion([Q0]), "operationType" : NewBodyOperationType.REMOVE, "endBound" : BoundingType.THROUGH_ALL, "oppositeDirection" : true, "depth" : 25 * mm, "hasSecondDirection" : true, "secondDirectionBound" : SecondDirectionBoundingType.THROUGH_ALL, "secondDirectionOppositeDirection" : false, "secondDirectionDepth" : 25 * mm});
        }
    });
